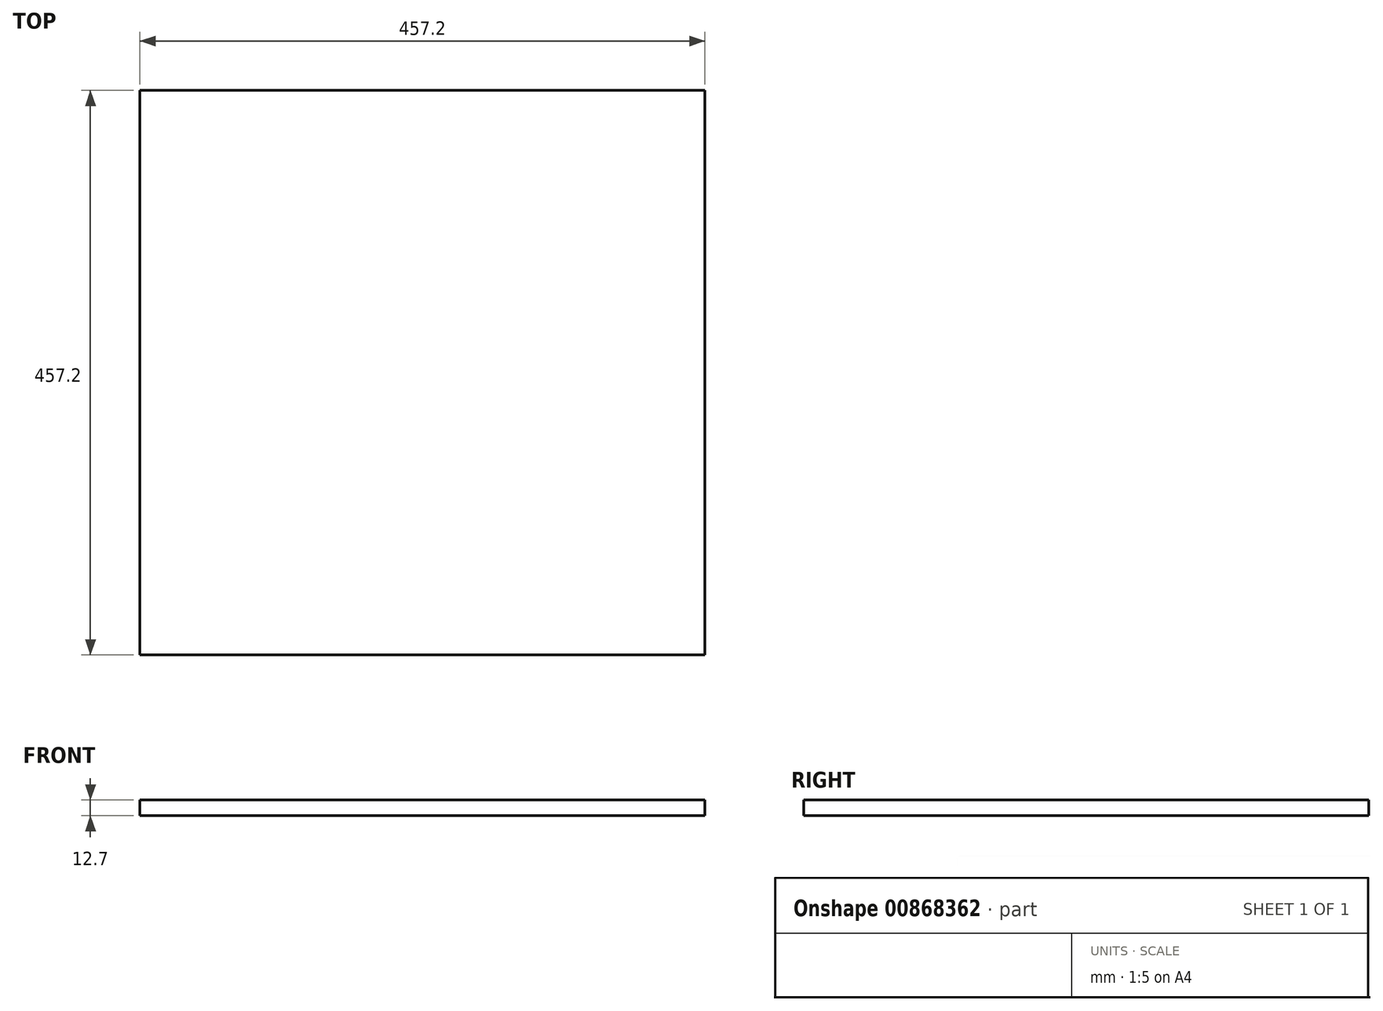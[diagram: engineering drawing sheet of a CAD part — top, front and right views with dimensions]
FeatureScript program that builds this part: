
annotation { "Feature Type Name" : "Feature", "Feature Type Description" : "" }
export const myFeature = defineFeature(function(context is Context, id is Id, definition is map)
    precondition{}
    {
        {
            var Q0;
            Q0=qCreatedBy(makeId("Top.planeOp"),FACE);
            var sketch = newSketch(context, id + "F0", { "sketchPlane" : qUnion([Q0])});
            skLineSegment(sketch, "E0.bottom", {"start": v(223.78, -228.6) * mm, "end": v(-233.42, -228.6) * mm});
            skLineSegment(sketch, "E0.top", {"start": v(223.78, 228.6) * mm, "end": v(-233.42, 228.6) * mm});
            skLineSegment(sketch, "E0.left", {"start": v(223.78, -228.6) * mm, "end": v(223.78, 228.6) * mm});
            skLineSegment(sketch, "E0.right", {"start": v(-233.42, -228.6) * mm, "end": v(-233.42, 228.6) * mm});
            skPoint(sketch, "E0.middle", {"position": v(-4.82, 0) * mm});
            skSolve(sketch);
        }
        {
            var Q0;
            Q0=makeQuery(id+"F0.imprint","IMPRINT",FACE,{"disambiguationData":[TD([[makeQuery(id+"F0.imprint","IMPRINT",EDGE,{"derivedFrom":sQuery(id+"F0.wireOp",EDGE,"E0.bottom")}),-1.0]])]});
            extrude(context, id + "F1", {"entities" : qUnion([Q0]), "depth" : 12.7 * mm, "offsetDistance" : 25.4 * mm});
        }
    });
